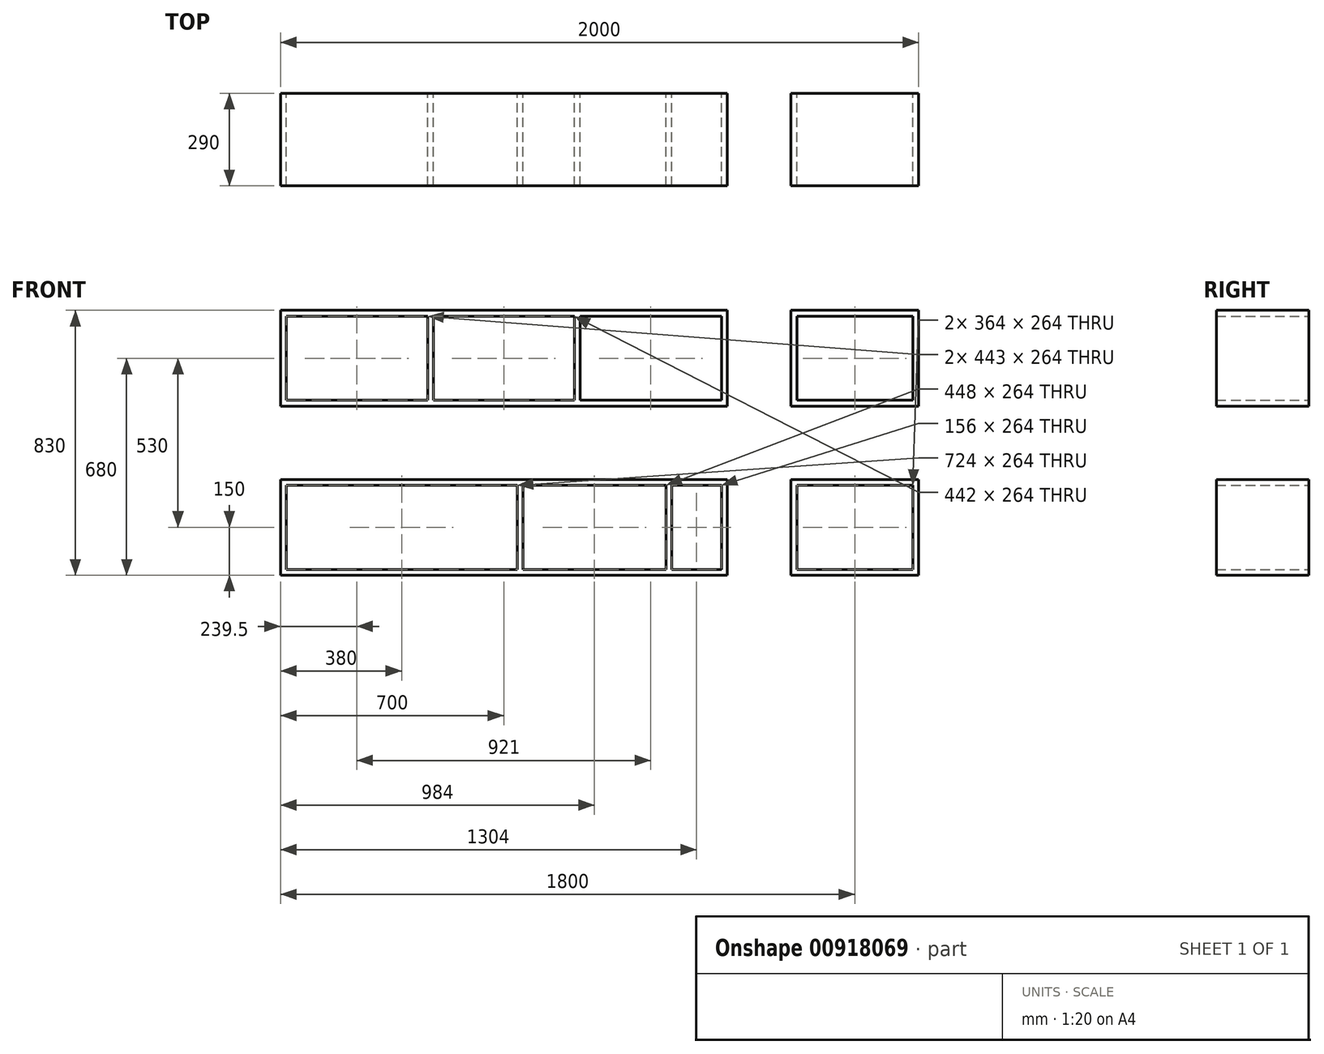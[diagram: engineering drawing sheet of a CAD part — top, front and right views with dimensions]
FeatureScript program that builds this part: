
annotation { "Feature Type Name" : "Feature", "Feature Type Description" : "" }
export const myFeature = defineFeature(function(context is Context, id is Id, definition is map)
    precondition{}
    {
        {
            var Q0;
            Q0=qCreatedBy(makeId("Front.planeOp"),FACE);
            var sketch = newSketch(context, id + "F0", { "sketchPlane" : qUnion([Q0])});
            skLineSegment(sketch, "E0.bottom", {"start": v(0, 0) * mm, "end": v(1400, 0) * mm});
            skLineSegment(sketch, "E0.top", {"start": v(0, 300) * mm, "end": v(1400, 300) * mm});
            skLineSegment(sketch, "E0.left", {"start": v(0, 0) * mm, "end": v(0, 300) * mm});
            skLineSegment(sketch, "E0.right", {"start": v(1400, 0) * mm, "end": v(1400, 300) * mm});
            skLineSegment(sketch, "E1.0", {"start": v(18, 18) * mm, "end": v(461, 18) * mm});
            skLineSegment(sketch, "E1.1", {"start": v(18, 18) * mm, "end": v(18, 282) * mm});
            skLineSegment(sketch, "E1.2", {"start": v(18, 282) * mm, "end": v(461, 282) * mm});
            skLineSegment(sketch, "E1.3", {"start": v(1382, 18) * mm, "end": v(1382, 282) * mm});
            skLineSegment(sketch, "E2.0", {"start": v(461, 18) * mm, "end": v(461, 282) * mm});
            skLineSegment(sketch, "E3.0", {"start": v(939, 18) * mm, "end": v(939, 282) * mm});
            skLineSegment(sketch, "E4.0", {"start": v(479, 18) * mm, "end": v(479, 282) * mm});
            skLineSegment(sketch, "E5.0", {"start": v(921, 18) * mm, "end": v(921, 282) * mm});
            skLineSegment(sketch, "E6.trimOffspring", {"start": v(479, 282) * mm, "end": v(921, 282) * mm});
            skLineSegment(sketch, "E7.trimOffspring", {"start": v(939, 282) * mm, "end": v(1382, 282) * mm});
            skLineSegment(sketch, "E8.trimOffspring", {"start": v(479, 18) * mm, "end": v(921, 18) * mm});
            skLineSegment(sketch, "E9.trimOffspring", {"start": v(939, 18) * mm, "end": v(1382, 18) * mm});
            skLineSegment(sketch, "E10.bottom", {"start": v(1600, 0) * mm, "end": v(2000, 0) * mm});
            skLineSegment(sketch, "E10.top", {"start": v(1600, 300) * mm, "end": v(2000, 300) * mm});
            skLineSegment(sketch, "E10.left", {"start": v(1600, 0) * mm, "end": v(1600, 300) * mm});
            skLineSegment(sketch, "E10.right", {"start": v(2000, 0) * mm, "end": v(2000, 300) * mm});
            skLineSegment(sketch, "E11.0", {"start": v(1982, 18) * mm, "end": v(1982, 282) * mm});
            skLineSegment(sketch, "E11.1", {"start": v(1618, 18) * mm, "end": v(1982, 18) * mm});
            skLineSegment(sketch, "E11.2", {"start": v(1618, 18) * mm, "end": v(1618, 282) * mm});
            skLineSegment(sketch, "E11.3", {"start": v(1618, 282) * mm, "end": v(1982, 282) * mm});
            skLineSegment(sketch, "E12.0.1.0", {"start": v(1600, -530) * mm, "end": v(1600, -230) * mm});
            skLineSegment(sketch, "E12.0.1.1", {"start": v(1982, -512) * mm, "end": v(1982, -248) * mm});
            skLineSegment(sketch, "E12.0.1.2", {"start": v(1618, -512) * mm, "end": v(1618, -248) * mm});
            skLineSegment(sketch, "E12.0.1.3", {"start": v(1208, -512) * mm, "end": v(1208, -248) * mm});
            skLineSegment(sketch, "E12.0.1.4", {"start": v(939, -512) * mm, "end": v(1208, -512) * mm});
            skLineSegment(sketch, "E12.0.1.5", {"start": v(0, -530) * mm, "end": v(1400, -530) * mm});
            skLineSegment(sketch, "E12.0.1.6", {"start": v(742, -512) * mm, "end": v(742, -248) * mm});
            skLineSegment(sketch, "E12.0.1.7", {"start": v(1400, -530) * mm, "end": v(1400, -230) * mm});
            skLineSegment(sketch, "E12.0.1.8", {"start": v(2000, -530) * mm, "end": v(2000, -230) * mm});
            skLineSegment(sketch, "E12.0.1.9", {"start": v(1618, -248) * mm, "end": v(1982, -248) * mm});
            skLineSegment(sketch, "E12.0.1.10", {"start": v(1618, -512) * mm, "end": v(1982, -512) * mm});
            skLineSegment(sketch, "E12.0.1.11", {"start": v(18, -248) * mm, "end": v(479, -248) * mm});
            skLineSegment(sketch, "E12.0.1.12", {"start": v(760, -512) * mm, "end": v(760, -248) * mm});
            skLineSegment(sketch, "E12.0.1.13", {"start": v(1600, -230) * mm, "end": v(2000, -230) * mm});
            skLineSegment(sketch, "E12.0.1.14", {"start": v(0, -230) * mm, "end": v(1400, -230) * mm});
            skLineSegment(sketch, "E12.0.1.15", {"start": v(0, -530) * mm, "end": v(0, -230) * mm});
            skLineSegment(sketch, "E12.0.1.16", {"start": v(18, -512) * mm, "end": v(18, -248) * mm});
            skLineSegment(sketch, "E12.0.1.17", {"start": v(1226, -512) * mm, "end": v(1226, -248) * mm});
            skLineSegment(sketch, "E12.0.1.18", {"start": v(479, -512) * mm, "end": v(742, -512) * mm});
            skLineSegment(sketch, "E12.0.1.19", {"start": v(1382, -512) * mm, "end": v(1382, -248) * mm});
            skLineSegment(sketch, "E12.0.1.20", {"start": v(18, -512) * mm, "end": v(479, -512) * mm});
            skLineSegment(sketch, "E12.0.1.21", {"start": v(479, -248) * mm, "end": v(742, -248) * mm});
            skLineSegment(sketch, "E12.0.1.22", {"start": v(1600, -530) * mm, "end": v(2000, -530) * mm});
            skLineSegment(sketch, "E12.0.1.23", {"start": v(939, -248) * mm, "end": v(1208, -248) * mm});
            skLineSegment(sketch, "E12.direction1", {"start": v(0, 0) * mm, "end": v(359, 0) * mm, "construction": true});
            skLineSegment(sketch, "E12.direction2", {"start": v(0, 0) * mm, "end": v(0, -530) * mm, "construction": true});
            skLineSegment(sketch, "E13.trimOffspring", {"start": v(1226, -248) * mm, "end": v(1382, -248) * mm});
            skLineSegment(sketch, "E14.trimOffspring", {"start": v(760, -248) * mm, "end": v(939, -248) * mm});
            skLineSegment(sketch, "E15.trimOffspring", {"start": v(760, -512) * mm, "end": v(939, -512) * mm});
            skLineSegment(sketch, "E16.trimOffspring", {"start": v(1226, -512) * mm, "end": v(1382, -512) * mm});
            skSolve(sketch);
        }
        {
            var Q0;
            Q0=makeQuery(id+"F0.imprint","IMPRINT",FACE,{"disambiguationData":[TD([[makeQuery(id+"F0.imprint","IMPRINT",EDGE,{"derivedFrom":sQuery(id+"F0.wireOp",EDGE,"E0.bottom")}),1.0]])]});
            var Q1;
            Q1=makeQuery(id+"F0.imprint","IMPRINT",FACE,{"disambiguationData":[TD([[makeQuery(id+"F0.imprint","IMPRINT",EDGE,{"derivedFrom":sQuery(id+"F0.wireOp",EDGE,"E10.bottom")}),1.0]])]});
            var Q2;
            Q2=makeQuery(id+"F0.imprint","IMPRINT",FACE,{"disambiguationData":[TD([[makeQuery(id+"F0.imprint","IMPRINT",EDGE,{"derivedFrom":sQuery(id+"F0.wireOp",EDGE,"E12.0.1.3")}),-1.0]])]});
            var Q3;
            Q3=makeQuery(id+"F0.imprint","IMPRINT",FACE,{"disambiguationData":[TD([[makeQuery(id+"F0.imprint","IMPRINT",EDGE,{"derivedFrom":sQuery(id+"F0.wireOp",EDGE,"E12.0.1.0")}),-1.0]])]});
            extrude(context, id + "F1", {"entities" : qUnion([Q0, Q1, Q2, Q3]), "depth" : 290 * mm, "offsetDistance" : 25 * mm});
        }
    });
